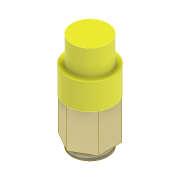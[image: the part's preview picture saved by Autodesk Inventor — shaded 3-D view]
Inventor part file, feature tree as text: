
AUTODESK INVENTOR PART (.ipt)
format: ipt  version: 2022 (Build 260153000, 153)  size: 113,152 bytes
history: native  units: mm
features: extrude x4, sketch x4, thread x1
ambient origin geometry x8: Origin, YZ Plane, XZ Plane, XY Plane, X Axis, Y Axis, Z Axis, Center Point
bodies: Solid1 (feature_tree), Solid2 (feature_tree)
feature tree (9):
  extrude  "Extrusion1"  Depth=3.0mm TaperAngle=0.0deg
  extrude  "Extrusion2"  Depth=3.0mm TaperAngle=0.0deg
  thread  "Thread1"  [1 undecoded]
  extrude  "Extrusion3"  [1 undecoded]
  extrude  "Extrusion4"  [1 undecoded]
  sketch  "Sketch1"  dims[d0=14.0mm d1=3.0mm d2=0.0mm]
  sketch  "Sketch2"  dims[d3=15.0mm d4=0.0mm d5=3.0mm d6=0.0mm d7=10.0mm d8=0.0mm]
  sketch  "Sketch3"  dims[d9=10.0mm d10=0.0mm]
  sketch  "Sketch4"
note: 3 required parameter values undecoded (feature->parameter linkage not recoverable at this tier; creation-order binding heuristic only, values carry confidence <= 0.55)
